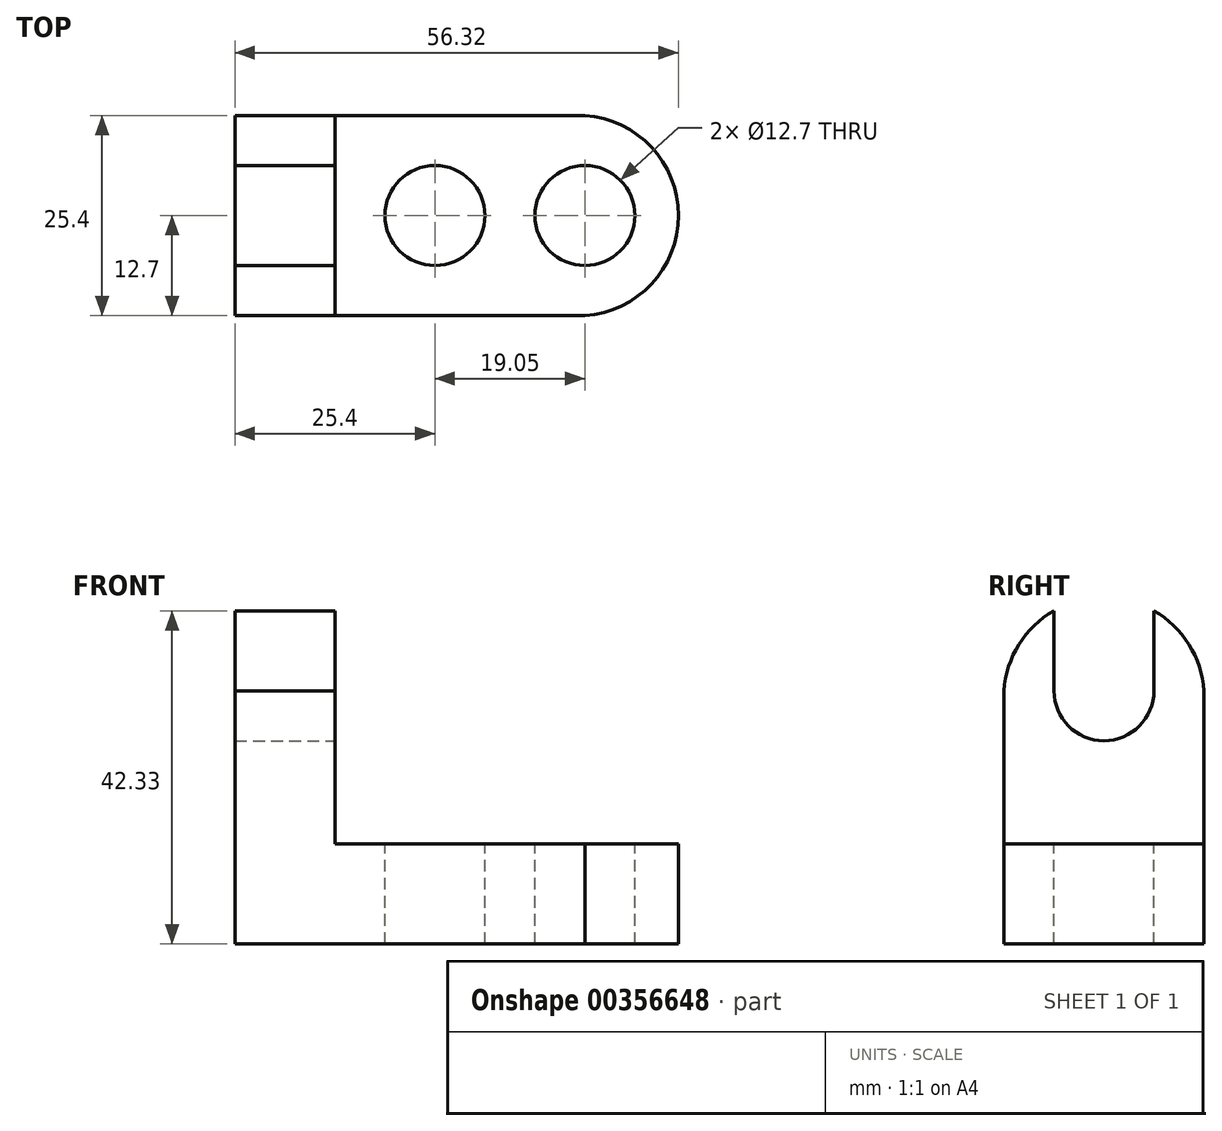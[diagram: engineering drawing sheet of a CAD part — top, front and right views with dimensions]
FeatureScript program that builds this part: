
annotation { "Feature Type Name" : "Feature", "Feature Type Description" : "" }
export const myFeature = defineFeature(function(context is Context, id is Id, definition is map)
    precondition{}
    {
        {
            var Q0;
            Q0=qCreatedBy(makeId("Front.planeOp"),FACE);
            var sketch = newSketch(context, id + "F0", { "sketchPlane" : qUnion([Q0])});
            skLineSegment(sketch, "E0", {"start": v(0, 0) * mm, "end": v(57.15, 0) * mm});
            skLineSegment(sketch, "E1", {"start": v(57.15, 0) * mm, "end": v(57.15, 12.7) * mm});
            skLineSegment(sketch, "E2", {"start": v(57.15, 12.7) * mm, "end": v(12.7, 12.7) * mm});
            skLineSegment(sketch, "E3", {"start": v(12.7, 12.7) * mm, "end": v(12.7, 44.45) * mm});
            skLineSegment(sketch, "E4", {"start": v(12.7, 44.45) * mm, "end": v(0, 44.45) * mm});
            skLineSegment(sketch, "E5", {"start": v(0, 44.45) * mm, "end": v(0, 0) * mm});
            skSolve(sketch);
        }
        {
            var Q0;
            Q0=makeQuery(id+"F0.imprint","IMPRINT",FACE,{"disambiguationData":[TD([[makeQuery(id+"F0.imprint","IMPRINT",EDGE,{"derivedFrom":sQuery(id+"F0.wireOp",EDGE,"E0")}),1.0]])]});
            extrude(context, id + "F1", {"entities" : qUnion([Q0]), "depth" : 25.4 * mm});
        }
        {
            var Q0;
            Q0=makeQuery(id+"F1.opExtrude","SWEPT_FACE",FACE,{"disambiguationData":[OSD([sQuery(id+"F0.wireOp",EDGE,"E3")])]});
            var sketch = newSketch(context, id + "F2", { "sketchPlane" : qUnion([Q0])});
            skCircle(sketch, "E6", {"center": v(-12.7, 32.16) * mm, "radius": 6.35 * mm});
            skPoint(sketch, "E6.centerSnap0", {"position": v(-12.7, 44.45) * mm});
            skLineSegment(sketch, "E7", {"start": v(-19.05, 32.16) * mm, "end": v(-19.05, 44.45) * mm});
            skLineSegment(sketch, "E8", {"start": v(-6.35, 32.16) * mm, "end": v(-6.35, 44.45) * mm});
            skArc(sketch, "E9", {"start": v(0, 32.16) * mm, "mid": v(-12.7, 44.02) * mm, "end": v(-25.4, 32.16) * mm});
            skSolve(sketch);
        }
        {
            var Q0;
            {var subQ1=sQuery(id+"F0.wireOp",EDGE,"E3");var subQ4=sQuery(id+"F2.wireOp",EDGE,"E9");var subQ6=makeQuery(id+"F1.opExtrude","CAP_EDGE",EDGE,{"disambiguationData":[OSD([subQ1])],"isStart":false});var subQ7=makeQuery(id+"F2.imprint","INTERSECT",VERTEX,{"derivedFrom":[subQ6,subQ4]});Q0=makeQuery(id+"F2.imprint","IMPRINT",FACE,{"disambiguationData":[TD([[makeQuery(id+"F2.imprint","IMPRINT",EDGE,{"disambiguationData":[TD([[subQ7,1.0]])],"derivedFrom":subQ4}),-1.0]])]});}
            var Q1;
            {var subQ0=sQuery(id+"F2.wireOp",EDGE,"E7");var subQ1=sQuery(id+"F2.wireOp",EDGE,"E6");var subQ2=makeQuery(id+"F2.imprint","INTERSECT",VERTEX,{"derivedFrom":[subQ1,subQ0]});Q1=makeQuery(id+"F2.imprint","IMPRINT",FACE,{"disambiguationData":[TD([[makeQuery(id+"F2.imprint","IMPRINT",EDGE,{"disambiguationData":[TD([[subQ2,1.0]])],"derivedFrom":subQ1}),-1.0]])]});}
            var Q2;
            {var subQ0=sQuery(id+"F2.wireOp",EDGE,"E7");var subQ3=sQuery(id+"F2.wireOp",EDGE,"E9");var subQ4=makeQuery(id+"F2.imprint","INTERSECT",VERTEX,{"derivedFrom":[subQ0,subQ3]});Q2=makeQuery(id+"F2.imprint","IMPRINT",FACE,{"disambiguationData":[TD([[makeQuery(id+"F2.imprint","IMPRINT",EDGE,{"disambiguationData":[TD([[subQ4,1.0]])],"derivedFrom":subQ3}),-1.0]])]});}
            var Q3;
            {var subQ0=sQuery(id+"F2.wireOp",EDGE,"E6");var subQ1=makeQuery(id+"F2.imprint","INTERSECT",VERTEX,{"derivedFrom":[subQ0,sQuery(id+"F2.wireOp",EDGE,"E7")]});Q3=makeQuery(id+"F2.imprint","IMPRINT",FACE,{"disambiguationData":[TD([[makeQuery(id+"F2.imprint","IMPRINT",EDGE,{"disambiguationData":[TD([[subQ1,1.0]])],"derivedFrom":subQ0}),1.0]])]});}
            var Q4;
            {var subQ1=sQuery(id+"F0.wireOp",EDGE,"E3");var subQ4=sQuery(id+"F2.wireOp",EDGE,"E9");var subQ6=makeQuery(id+"F1.opExtrude","CAP_EDGE",EDGE,{"disambiguationData":[OSD([subQ1])],"isStart":true});var subQ8=makeQuery(id+"F2.imprint","INTERSECT",VERTEX,{"derivedFrom":[subQ6,subQ4]});Q4=makeQuery(id+"F2.imprint","IMPRINT",FACE,{"disambiguationData":[TD([[makeQuery(id+"F2.imprint","IMPRINT",EDGE,{"disambiguationData":[TD([[subQ8,-1.0]])],"derivedFrom":subQ4}),-1.0]])]});}
            extrude(context, id + "F3", {"entities" : qUnion([Q0, Q1, Q2, Q3, Q4]), "operationType" : NewBodyOperationType.REMOVE, "oppositeDirection" : true, "depth" : 25.4 * mm});
        }
        {
            var Q0;
            Q0=makeQuery(id+"F1.opExtrude","SWEPT_FACE",FACE,{"disambiguationData":[OSD([sQuery(id+"F0.wireOp",EDGE,"E2")])]});
            var sketch = newSketch(context, id + "F4", { "sketchPlane" : qUnion([Q0])});
            skCircle(sketch, "E10", {"center": v(25.4, -12.7) * mm, "radius": 6.35 * mm});
            skCircle(sketch, "E11", {"center": v(44.45, -12.7) * mm, "radius": 6.35 * mm});
            skArc(sketch, "E12", {"start": v(44.45, -25.4) * mm, "mid": v(56.32, -12.7) * mm, "end": v(44.45, 0) * mm});
            skSolve(sketch);
        }
        {
            var Q0;
            Q0=makeQuery(id+"F4.imprint","IMPRINT",FACE,{"disambiguationData":[TD([[makeQuery(id+"F4.imprint","IMPRINT",EDGE,{"derivedFrom":sQuery(id+"F4.wireOp",EDGE,"E10")}),1.0]])]});
            var Q1;
            Q1=makeQuery(id+"F4.imprint","IMPRINT",FACE,{"disambiguationData":[TD([[makeQuery(id+"F4.imprint","IMPRINT",EDGE,{"derivedFrom":sQuery(id+"F4.wireOp",EDGE,"E11")}),1.0]])]});
            var Q2;
            {var subQ0=sQuery(id+"F4.wireOp",EDGE,"E12");Q2=makeQuery(id+"F4.imprint","IMPRINT",FACE,{"disambiguationData":[TD([[makeQuery(id+"F4.imprint","IMPRINT",EDGE,{"derivedFrom":subQ0}),-1.0]])]});}
            extrude(context, id + "F5", {"entities" : qUnion([Q0, Q1, Q2]), "operationType" : NewBodyOperationType.REMOVE, "oppositeDirection" : true, "depth" : 25.4 * mm});
        }
    });
